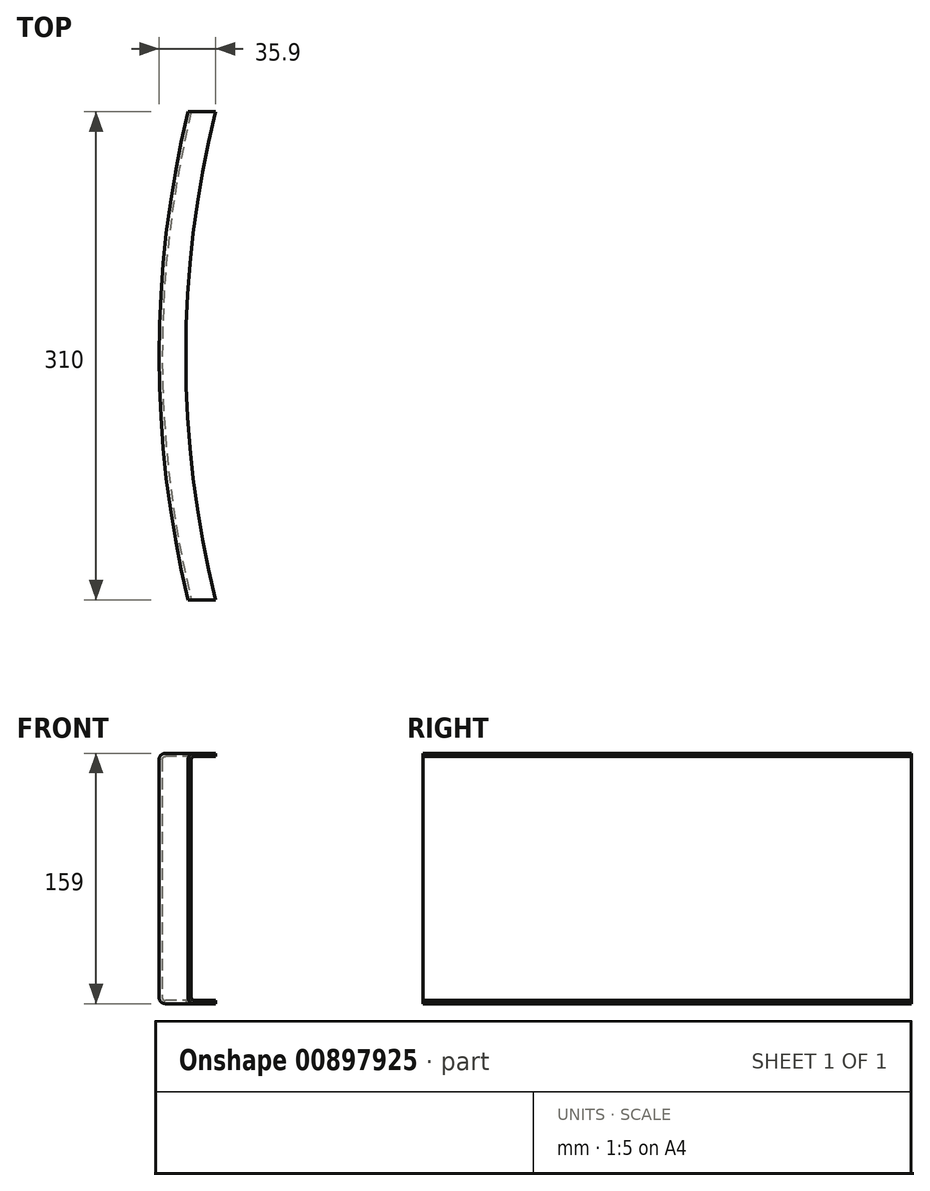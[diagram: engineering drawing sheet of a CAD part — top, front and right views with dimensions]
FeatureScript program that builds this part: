
annotation { "Feature Type Name" : "Feature", "Feature Type Description" : "" }
export const myFeature = defineFeature(function(context is Context, id is Id, definition is map)
    precondition{}
    {
        {
            var Q0;
            Q0=qCreatedBy(makeId("Right.planeOp"),FACE);
            var sketch = newSketch(context, id + "F0", { "sketchPlane" : qUnion([Q0])});
            skLineSegment(sketch, "E0", {"start": v(-645, 77.5) * mm, "end": v(-658, 77.5) * mm});
            skLineSegment(sketch, "E1", {"start": v(-660, 75.5) * mm, "end": v(-660, -75.5) * mm});
            skLineSegment(sketch, "E2", {"start": v(-658, -77.5) * mm, "end": v(-645, -77.5) * mm});
            skLineSegment(sketch, "E3", {"start": v(0, 0) * mm, "end": v(-660, 0) * mm, "construction": true});
            skLineSegment(sketch, "E4.0", {"start": v(-658, -79.5) * mm, "end": v(-645, -79.5) * mm});
            skLineSegment(sketch, "E4.1", {"start": v(-662, 75.5) * mm, "end": v(-662, -75.5) * mm});
            skLineSegment(sketch, "E4.2", {"start": v(-645, 79.5) * mm, "end": v(-658, 79.5) * mm});
            skLineSegment(sketch, "E5", {"start": v(-645, 77.5) * mm, "end": v(-645, 79.5) * mm});
            skLineSegment(sketch, "E6", {"start": v(-645, -79.5) * mm, "end": v(-645, -77.5) * mm});
            skPoint(sketch, "E7.visualSharp", {"position": v(-660, 77.5) * mm});
            skArc(sketch, "E7.filletArc", {"start": v(-658, 77.5) * mm, "mid": v(-659.41, 76.91) * mm, "end": v(-660, 75.5) * mm});
            skPoint(sketch, "E8.visualSharp", {"position": v(-660, -77.5) * mm});
            skArc(sketch, "E8.filletArc", {"start": v(-660, -75.5) * mm, "mid": v(-659.41, -76.91) * mm, "end": v(-658, -77.5) * mm});
            skPoint(sketch, "E9.visualSharp", {"position": v(-662, 79.5) * mm});
            skArc(sketch, "E9.filletArc", {"start": v(-658, 79.5) * mm, "mid": v(-660.83, 78.33) * mm, "end": v(-662, 75.5) * mm});
            skPoint(sketch, "E10.visualSharp", {"position": v(-662, -79.5) * mm});
            skArc(sketch, "E10.filletArc", {"start": v(-662, -75.5) * mm, "mid": v(-660.83, -78.33) * mm, "end": v(-658, -79.5) * mm});
            skSolve(sketch);
        }
        {
            var Q0;
            Q0=qCreatedBy(makeId("Top.planeOp"),FACE);
            var sketch = newSketch(context, id + "F1", { "sketchPlane" : qUnion([Q0])});
            skArc(sketch, "E11", {"start": v(0, 660) * mm, "mid": v(-660, 0) * mm, "end": v(0, -660) * mm});
            skSolve(sketch);
        }
        {
            var Q0;
            Q0=makeQuery(id+"F0.imprint","IMPRINT",FACE,{"disambiguationData":[TD([[makeQuery(id+"F0.imprint","IMPRINT",EDGE,{"derivedFrom":sQuery(id+"F0.wireOp",EDGE,"E0")}),-1.0]])]});
            var Q1;
            Q1=sQuery(id+"F1.wireOp",EDGE,"E11");
            sweep(context, id + "F2", {"profiles" : qUnion([Q0]), "path" : qUnion([Q1])});
        }
        {
            var Q0;
            Q0=qCreatedBy(makeId("Top.planeOp"),FACE);
            var sketch = newSketch(context, id + "F3", { "sketchPlane" : qUnion([Q0])});
            skLineSegment(sketch, "E12.bottom", {"start": v(-155, -662) * mm, "end": v(155, -662) * mm});
            skLineSegment(sketch, "E12.top", {"start": v(-155, 662) * mm, "end": v(155, 662) * mm});
            skLineSegment(sketch, "E12.left", {"start": v(-155, -662) * mm, "end": v(-155, 662) * mm});
            skLineSegment(sketch, "E12.right", {"start": v(155, -662) * mm, "end": v(155, 662) * mm});
            skPoint(sketch, "E12.middle", {"position": v(0, 0) * mm});
            skSolve(sketch);
        }
        {
            var Q0;
            Q0=qSketchRegion(id+"F3",true);
            extrude(context, id + "F4", {"entities" : qUnion([Q0]), "operationType" : NewBodyOperationType.REMOVE, "endBound" : BoundingType.SYMMETRIC, "oppositeDirection" : true, "depth" : 200 * mm, "offsetDistance" : 25 * mm});
        }
        {
            var Q0;
            Q0=qCreatedBy(makeId("Top.planeOp"),FACE);
            var sketch = newSketch(context, id + "F5", { "sketchPlane" : qUnion([Q0])});
            skLineSegment(sketch, "E13.bottom", {"start": v(-662, 155) * mm, "end": v(662, 155) * mm});
            skLineSegment(sketch, "E13.top", {"start": v(-662, 643.6) * mm, "end": v(662, 643.6) * mm});
            skLineSegment(sketch, "E13.left", {"start": v(-662, 155) * mm, "end": v(-662, 643.6) * mm});
            skLineSegment(sketch, "E13.right", {"start": v(662, 155) * mm, "end": v(662, 643.6) * mm});
            skPoint(sketch, "E13.middle", {"position": v(0, 399.3) * mm});
            skLineSegment(sketch, "E14.bottom", {"start": v(-662, -643.6) * mm, "end": v(662, -643.6) * mm});
            skLineSegment(sketch, "E14.top", {"start": v(-662, -155) * mm, "end": v(662, -155) * mm});
            skLineSegment(sketch, "E14.left", {"start": v(-662, -643.6) * mm, "end": v(-662, -155) * mm});
            skLineSegment(sketch, "E14.right", {"start": v(662, -643.6) * mm, "end": v(662, -155) * mm});
            skPoint(sketch, "E14.middle", {"position": v(0, -399.3) * mm});
            skSolve(sketch);
        }
        {
            var Q0;
            Q0=qSketchRegion(id+"F5",true);
            extrude(context, id + "F6", {"entities" : qUnion([Q0]), "operationType" : NewBodyOperationType.REMOVE, "endBound" : BoundingType.SYMMETRIC, "oppositeDirection" : true, "depth" : 200 * mm, "offsetDistance" : 25 * mm});
        }
    });
